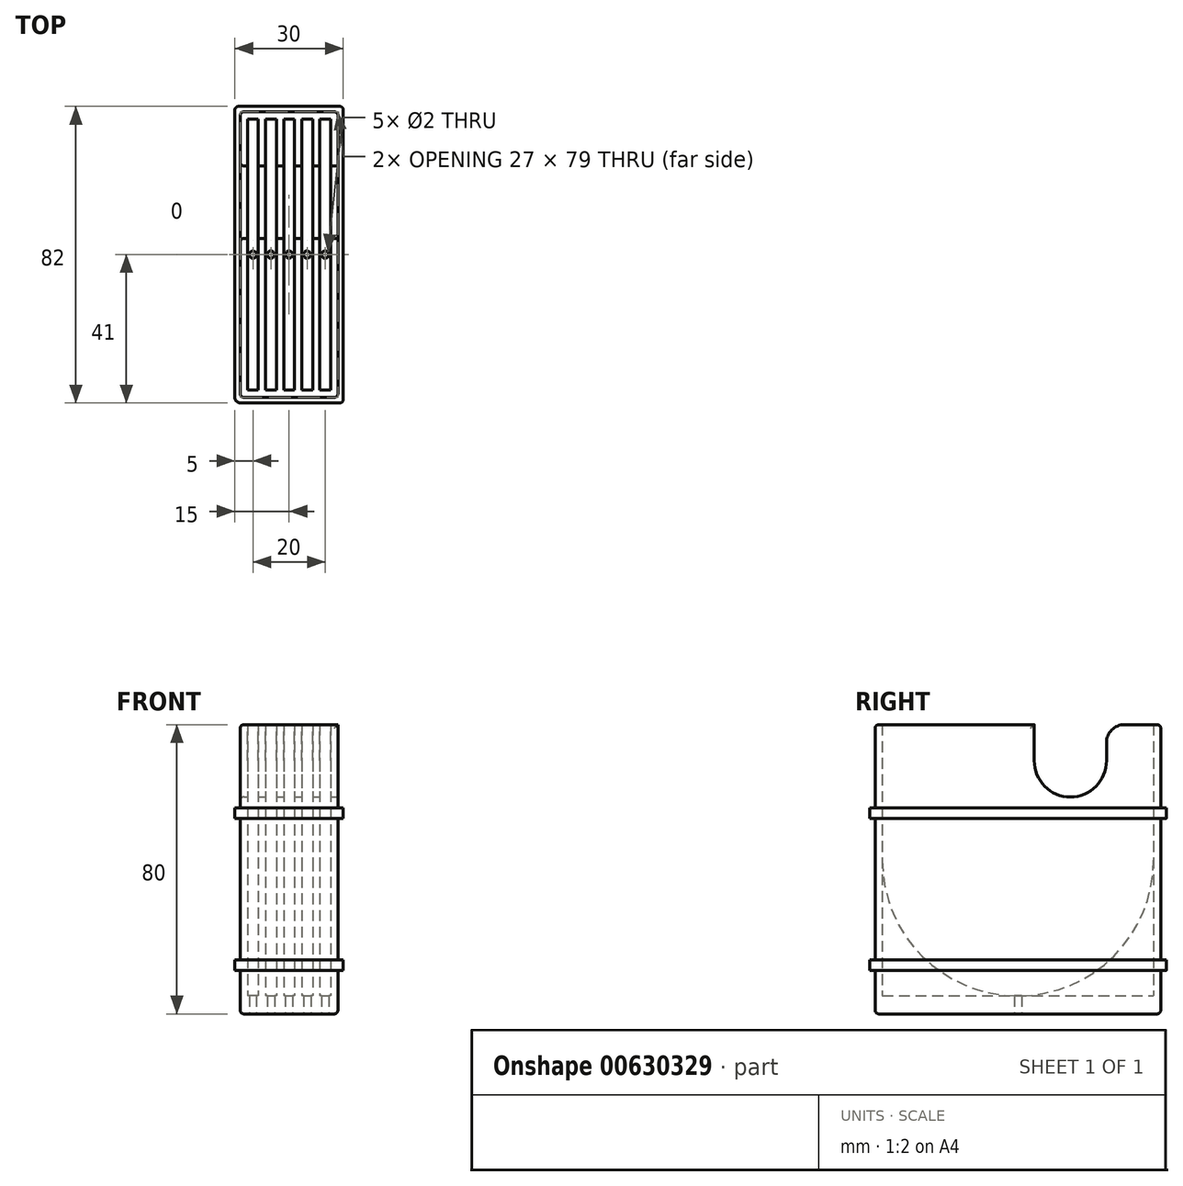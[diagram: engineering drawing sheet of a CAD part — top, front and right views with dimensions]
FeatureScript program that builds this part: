
annotation { "Feature Type Name" : "Feature", "Feature Type Description" : "" }
export const myFeature = defineFeature(function(context is Context, id is Id, definition is map)
    precondition{}
    {
        {
            var Q0;
            Q0=qCreatedBy(makeId("Top.planeOp"),FACE);
            var sketch = newSketch(context, id + "F0", { "sketchPlane" : qUnion([Q0])});
            skLineSegment(sketch, "E0.bottom", {"start": v(0, 0) * mm, "end": v(-3, 0) * mm});
            skLineSegment(sketch, "E0.top", {"start": v(0, 75) * mm, "end": v(-3, 75) * mm});
            skLineSegment(sketch, "E0.left", {"start": v(0, 0) * mm, "end": v(0, 75) * mm});
            skLineSegment(sketch, "E0.right", {"start": v(-3, 0) * mm, "end": v(-3, 75) * mm});
            skLineSegment(sketch, "E1.1.0.0", {"start": v(2, 0) * mm, "end": v(2, 75) * mm});
            skLineSegment(sketch, "E1.1.0.1", {"start": v(5, 75) * mm, "end": v(2, 75) * mm});
            skLineSegment(sketch, "E1.1.0.2", {"start": v(5, 0) * mm, "end": v(5, 75) * mm});
            skLineSegment(sketch, "E1.1.0.3", {"start": v(5, 0) * mm, "end": v(2, 0) * mm});
            skLineSegment(sketch, "E1.2.0.0", {"start": v(7, 0) * mm, "end": v(7, 75) * mm});
            skLineSegment(sketch, "E1.2.0.1", {"start": v(10, 75) * mm, "end": v(7, 75) * mm});
            skLineSegment(sketch, "E1.2.0.2", {"start": v(10, 0) * mm, "end": v(10, 75) * mm});
            skLineSegment(sketch, "E1.2.0.3", {"start": v(10, 0) * mm, "end": v(7, 0) * mm});
            skLineSegment(sketch, "E1.3.0.0", {"start": v(12, 0) * mm, "end": v(12, 75) * mm});
            skLineSegment(sketch, "E1.3.0.1", {"start": v(15, 75) * mm, "end": v(12, 75) * mm});
            skLineSegment(sketch, "E1.3.0.2", {"start": v(15, 0) * mm, "end": v(15, 75) * mm});
            skLineSegment(sketch, "E1.3.0.3", {"start": v(15, 0) * mm, "end": v(12, 0) * mm});
            skLineSegment(sketch, "E1.4.0.0", {"start": v(17, 0) * mm, "end": v(17, 75) * mm});
            skLineSegment(sketch, "E1.4.0.1", {"start": v(20, 75) * mm, "end": v(17, 75) * mm});
            skLineSegment(sketch, "E1.4.0.2", {"start": v(20, 0) * mm, "end": v(20, 75) * mm});
            skLineSegment(sketch, "E1.4.0.3", {"start": v(20, 0) * mm, "end": v(17, 0) * mm});
            skLineSegment(sketch, "E1.direction1", {"start": v(-3, 0) * mm, "end": v(2, 0) * mm, "construction": true});
            skLineSegment(sketch, "E2", {"start": v(-3, 0) * mm, "end": v(-5, 0) * mm, "construction": true});
            skLineSegment(sketch, "E3", {"start": v(-5, 0) * mm, "end": v(-5, -2) * mm, "construction": true});
            skLineSegment(sketch, "E4.bottom", {"start": v(-5, -2) * mm, "end": v(22, -2) * mm});
            skLineSegment(sketch, "E4.top", {"start": v(-5, 77) * mm, "end": v(22, 77) * mm});
            skLineSegment(sketch, "E4.left", {"start": v(-5, -2) * mm, "end": v(-5, 77) * mm});
            skLineSegment(sketch, "E4.right", {"start": v(22, -2) * mm, "end": v(22, 77) * mm});
            skSolve(sketch);
        }
        {
            var Q0;
            Q0=makeQuery(id+"F0.imprint","IMPRINT",FACE,{"disambiguationData":[TD([[makeQuery(id+"F0.imprint","IMPRINT",EDGE,{"derivedFrom":sQuery(id+"F0.wireOp",EDGE,"E0.bottom")}),1.0]])]});
            extrude(context, id + "F1", {"entities" : qUnion([Q0]), "depth" : 75 * mm, "offsetDistance" : 25 * mm});
        }
        {
            var Q0;
            Q0=qCreatedBy(makeId("Right.planeOp"),FACE);
            var sketch = newSketch(context, id + "F2", { "sketchPlane" : qUnion([Q0])});
            skArc(sketch, "E5", {"start": v(42, 65) * mm, "mid": v(52, 55) * mm, "end": v(62, 65) * mm});
            skLineSegment(sketch, "E6", {"start": v(42, 65) * mm, "end": v(42, 77.98) * mm});
            skLineSegment(sketch, "E7", {"start": v(42, 77.98) * mm, "end": v(62, 77.98) * mm});
            skLineSegment(sketch, "E8", {"start": v(62, 77.98) * mm, "end": v(62, 65) * mm});
            skSolve(sketch);
        }
        {
            var Q0;
            Q0 = qSketchRegion(id + "F2", true);
            extrude(context, id + "F3", {"entities" : qUnion([Q0]), "operationType" : NewBodyOperationType.REMOVE, "oppositeDirection" : true, "depth" : 25 * mm, "offsetDistance" : 25 * mm, "hasSecondDirection" : true, "secondDirectionOppositeDirection" : false, "secondDirectionDepth" : 25 * mm});
        }
        {
            var Q0;
            Q0=makeQuery(id+"F3.boolean.opBoolean","INTERSECT",EDGE,{"disambiguationData":[OD(1.0)],"derivedFrom":[makeQuery(id+"F1.opExtrude","CAP_FACE",FACE,{"disambiguationData":[OSD([sQuery(id+"F0.wireOp",EDGE,"E0.bottom"),sQuery(id+"F0.wireOp",EDGE,"E0.top"),sQuery(id+"F0.wireOp",EDGE,"E0.left"),sQuery(id+"F0.wireOp",EDGE,"E0.right"),sQuery(id+"F0.wireOp",EDGE,"E1.1.0.0"),sQuery(id+"F0.wireOp",EDGE,"E1.1.0.1"),sQuery(id+"F0.wireOp",EDGE,"E1.1.0.2"),sQuery(id+"F0.wireOp",EDGE,"E1.1.0.3"),sQuery(id+"F0.wireOp",EDGE,"E1.2.0.0"),sQuery(id+"F0.wireOp",EDGE,"E1.2.0.1"),sQuery(id+"F0.wireOp",EDGE,"E1.2.0.2"),sQuery(id+"F0.wireOp",EDGE,"E1.2.0.3"),sQuery(id+"F0.wireOp",EDGE,"E1.3.0.0"),sQuery(id+"F0.wireOp",EDGE,"E1.3.0.1"),sQuery(id+"F0.wireOp",EDGE,"E1.3.0.2"),sQuery(id+"F0.wireOp",EDGE,"E1.3.0.3"),sQuery(id+"F0.wireOp",EDGE,"E1.4.0.0"),sQuery(id+"F0.wireOp",EDGE,"E1.4.0.1"),sQuery(id+"F0.wireOp",EDGE,"E1.4.0.2"),sQuery(id+"F0.wireOp",EDGE,"E1.4.0.3"),sQuery(id+"F0.wireOp",EDGE,"E4.bottom"),sQuery(id+"F0.wireOp",EDGE,"E4.top"),sQuery(id+"F0.wireOp",EDGE,"E4.left"),sQuery(id+"F0.wireOp",EDGE,"E4.right")])],"isStart":false}),makeQuery(id+"F3.opExtrude","SWEPT_FACE",FACE,{"disambiguationData":[OSD([sQuery(id+"F2.wireOp",EDGE,"E8")])]})]});
            var Q1;
            Q1=makeQuery(id+"F3.boolean.opBoolean","INTERSECT",EDGE,{"disambiguationData":[OD(0.0)],"derivedFrom":[makeQuery(id+"F1.opExtrude","CAP_FACE",FACE,{"disambiguationData":[OSD([sQuery(id+"F0.wireOp",EDGE,"E0.bottom"),sQuery(id+"F0.wireOp",EDGE,"E0.top"),sQuery(id+"F0.wireOp",EDGE,"E0.left"),sQuery(id+"F0.wireOp",EDGE,"E0.right"),sQuery(id+"F0.wireOp",EDGE,"E1.1.0.0"),sQuery(id+"F0.wireOp",EDGE,"E1.1.0.1"),sQuery(id+"F0.wireOp",EDGE,"E1.1.0.2"),sQuery(id+"F0.wireOp",EDGE,"E1.1.0.3"),sQuery(id+"F0.wireOp",EDGE,"E1.2.0.0"),sQuery(id+"F0.wireOp",EDGE,"E1.2.0.1"),sQuery(id+"F0.wireOp",EDGE,"E1.2.0.2"),sQuery(id+"F0.wireOp",EDGE,"E1.2.0.3"),sQuery(id+"F0.wireOp",EDGE,"E1.3.0.0"),sQuery(id+"F0.wireOp",EDGE,"E1.3.0.1"),sQuery(id+"F0.wireOp",EDGE,"E1.3.0.2"),sQuery(id+"F0.wireOp",EDGE,"E1.3.0.3"),sQuery(id+"F0.wireOp",EDGE,"E1.4.0.0"),sQuery(id+"F0.wireOp",EDGE,"E1.4.0.1"),sQuery(id+"F0.wireOp",EDGE,"E1.4.0.2"),sQuery(id+"F0.wireOp",EDGE,"E1.4.0.3"),sQuery(id+"F0.wireOp",EDGE,"E4.bottom"),sQuery(id+"F0.wireOp",EDGE,"E4.top"),sQuery(id+"F0.wireOp",EDGE,"E4.left"),sQuery(id+"F0.wireOp",EDGE,"E4.right")])],"isStart":false}),makeQuery(id+"F3.opExtrude","SWEPT_FACE",FACE,{"disambiguationData":[OSD([sQuery(id+"F2.wireOp",EDGE,"E8")])]})]});
            var Q2;
            Q2=makeQuery(id+"F3.boolean.opBoolean","INTERSECT",EDGE,{"disambiguationData":[OD(2.0)],"derivedFrom":[makeQuery(id+"F1.opExtrude","CAP_FACE",FACE,{"disambiguationData":[OSD([sQuery(id+"F0.wireOp",EDGE,"E0.bottom"),sQuery(id+"F0.wireOp",EDGE,"E0.top"),sQuery(id+"F0.wireOp",EDGE,"E0.left"),sQuery(id+"F0.wireOp",EDGE,"E0.right"),sQuery(id+"F0.wireOp",EDGE,"E1.1.0.0"),sQuery(id+"F0.wireOp",EDGE,"E1.1.0.1"),sQuery(id+"F0.wireOp",EDGE,"E1.1.0.2"),sQuery(id+"F0.wireOp",EDGE,"E1.1.0.3"),sQuery(id+"F0.wireOp",EDGE,"E1.2.0.0"),sQuery(id+"F0.wireOp",EDGE,"E1.2.0.1"),sQuery(id+"F0.wireOp",EDGE,"E1.2.0.2"),sQuery(id+"F0.wireOp",EDGE,"E1.2.0.3"),sQuery(id+"F0.wireOp",EDGE,"E1.3.0.0"),sQuery(id+"F0.wireOp",EDGE,"E1.3.0.1"),sQuery(id+"F0.wireOp",EDGE,"E1.3.0.2"),sQuery(id+"F0.wireOp",EDGE,"E1.3.0.3"),sQuery(id+"F0.wireOp",EDGE,"E1.4.0.0"),sQuery(id+"F0.wireOp",EDGE,"E1.4.0.1"),sQuery(id+"F0.wireOp",EDGE,"E1.4.0.2"),sQuery(id+"F0.wireOp",EDGE,"E1.4.0.3"),sQuery(id+"F0.wireOp",EDGE,"E4.bottom"),sQuery(id+"F0.wireOp",EDGE,"E4.top"),sQuery(id+"F0.wireOp",EDGE,"E4.left"),sQuery(id+"F0.wireOp",EDGE,"E4.right")])],"isStart":false}),makeQuery(id+"F3.opExtrude","SWEPT_FACE",FACE,{"disambiguationData":[OSD([sQuery(id+"F2.wireOp",EDGE,"E8")])]})]});
            var Q3;
            Q3=makeQuery(id+"F3.boolean.opBoolean","INTERSECT",EDGE,{"disambiguationData":[OD(3.0)],"derivedFrom":[makeQuery(id+"F1.opExtrude","CAP_FACE",FACE,{"disambiguationData":[OSD([sQuery(id+"F0.wireOp",EDGE,"E0.bottom"),sQuery(id+"F0.wireOp",EDGE,"E0.top"),sQuery(id+"F0.wireOp",EDGE,"E0.left"),sQuery(id+"F0.wireOp",EDGE,"E0.right"),sQuery(id+"F0.wireOp",EDGE,"E1.1.0.0"),sQuery(id+"F0.wireOp",EDGE,"E1.1.0.1"),sQuery(id+"F0.wireOp",EDGE,"E1.1.0.2"),sQuery(id+"F0.wireOp",EDGE,"E1.1.0.3"),sQuery(id+"F0.wireOp",EDGE,"E1.2.0.0"),sQuery(id+"F0.wireOp",EDGE,"E1.2.0.1"),sQuery(id+"F0.wireOp",EDGE,"E1.2.0.2"),sQuery(id+"F0.wireOp",EDGE,"E1.2.0.3"),sQuery(id+"F0.wireOp",EDGE,"E1.3.0.0"),sQuery(id+"F0.wireOp",EDGE,"E1.3.0.1"),sQuery(id+"F0.wireOp",EDGE,"E1.3.0.2"),sQuery(id+"F0.wireOp",EDGE,"E1.3.0.3"),sQuery(id+"F0.wireOp",EDGE,"E1.4.0.0"),sQuery(id+"F0.wireOp",EDGE,"E1.4.0.1"),sQuery(id+"F0.wireOp",EDGE,"E1.4.0.2"),sQuery(id+"F0.wireOp",EDGE,"E1.4.0.3"),sQuery(id+"F0.wireOp",EDGE,"E4.bottom"),sQuery(id+"F0.wireOp",EDGE,"E4.top"),sQuery(id+"F0.wireOp",EDGE,"E4.left"),sQuery(id+"F0.wireOp",EDGE,"E4.right")])],"isStart":false}),makeQuery(id+"F3.opExtrude","SWEPT_FACE",FACE,{"disambiguationData":[OSD([sQuery(id+"F2.wireOp",EDGE,"E8")])]})]});
            var Q4;
            Q4=makeQuery(id+"F3.boolean.opBoolean","INTERSECT",EDGE,{"disambiguationData":[OD(4.0)],"derivedFrom":[makeQuery(id+"F1.opExtrude","CAP_FACE",FACE,{"disambiguationData":[OSD([sQuery(id+"F0.wireOp",EDGE,"E0.bottom"),sQuery(id+"F0.wireOp",EDGE,"E0.top"),sQuery(id+"F0.wireOp",EDGE,"E0.left"),sQuery(id+"F0.wireOp",EDGE,"E0.right"),sQuery(id+"F0.wireOp",EDGE,"E1.1.0.0"),sQuery(id+"F0.wireOp",EDGE,"E1.1.0.1"),sQuery(id+"F0.wireOp",EDGE,"E1.1.0.2"),sQuery(id+"F0.wireOp",EDGE,"E1.1.0.3"),sQuery(id+"F0.wireOp",EDGE,"E1.2.0.0"),sQuery(id+"F0.wireOp",EDGE,"E1.2.0.1"),sQuery(id+"F0.wireOp",EDGE,"E1.2.0.2"),sQuery(id+"F0.wireOp",EDGE,"E1.2.0.3"),sQuery(id+"F0.wireOp",EDGE,"E1.3.0.0"),sQuery(id+"F0.wireOp",EDGE,"E1.3.0.1"),sQuery(id+"F0.wireOp",EDGE,"E1.3.0.2"),sQuery(id+"F0.wireOp",EDGE,"E1.3.0.3"),sQuery(id+"F0.wireOp",EDGE,"E1.4.0.0"),sQuery(id+"F0.wireOp",EDGE,"E1.4.0.1"),sQuery(id+"F0.wireOp",EDGE,"E1.4.0.2"),sQuery(id+"F0.wireOp",EDGE,"E1.4.0.3"),sQuery(id+"F0.wireOp",EDGE,"E4.bottom"),sQuery(id+"F0.wireOp",EDGE,"E4.top"),sQuery(id+"F0.wireOp",EDGE,"E4.left"),sQuery(id+"F0.wireOp",EDGE,"E4.right")])],"isStart":false}),makeQuery(id+"F3.opExtrude","SWEPT_FACE",FACE,{"disambiguationData":[OSD([sQuery(id+"F2.wireOp",EDGE,"E8")])]})]});
            var Q5;
            Q5=makeQuery(id+"F3.boolean.opBoolean","INTERSECT",EDGE,{"disambiguationData":[OD(5.0)],"derivedFrom":[makeQuery(id+"F1.opExtrude","CAP_FACE",FACE,{"disambiguationData":[OSD([sQuery(id+"F0.wireOp",EDGE,"E0.bottom"),sQuery(id+"F0.wireOp",EDGE,"E0.top"),sQuery(id+"F0.wireOp",EDGE,"E0.left"),sQuery(id+"F0.wireOp",EDGE,"E0.right"),sQuery(id+"F0.wireOp",EDGE,"E1.1.0.0"),sQuery(id+"F0.wireOp",EDGE,"E1.1.0.1"),sQuery(id+"F0.wireOp",EDGE,"E1.1.0.2"),sQuery(id+"F0.wireOp",EDGE,"E1.1.0.3"),sQuery(id+"F0.wireOp",EDGE,"E1.2.0.0"),sQuery(id+"F0.wireOp",EDGE,"E1.2.0.1"),sQuery(id+"F0.wireOp",EDGE,"E1.2.0.2"),sQuery(id+"F0.wireOp",EDGE,"E1.2.0.3"),sQuery(id+"F0.wireOp",EDGE,"E1.3.0.0"),sQuery(id+"F0.wireOp",EDGE,"E1.3.0.1"),sQuery(id+"F0.wireOp",EDGE,"E1.3.0.2"),sQuery(id+"F0.wireOp",EDGE,"E1.3.0.3"),sQuery(id+"F0.wireOp",EDGE,"E1.4.0.0"),sQuery(id+"F0.wireOp",EDGE,"E1.4.0.1"),sQuery(id+"F0.wireOp",EDGE,"E1.4.0.2"),sQuery(id+"F0.wireOp",EDGE,"E1.4.0.3"),sQuery(id+"F0.wireOp",EDGE,"E4.bottom"),sQuery(id+"F0.wireOp",EDGE,"E4.top"),sQuery(id+"F0.wireOp",EDGE,"E4.left"),sQuery(id+"F0.wireOp",EDGE,"E4.right")])],"isStart":false}),makeQuery(id+"F3.opExtrude","SWEPT_FACE",FACE,{"disambiguationData":[OSD([sQuery(id+"F2.wireOp",EDGE,"E8")])]})]});
            fillet(context, id + "F4", {"entities" : qUnion([Q0, Q1, Q2, Q3, Q4, Q5]), "radius" : 5 * mm, "tangentPropagation" : true, "allowEdgeOverflow" : false});
        }
        {
            var Q0;
            Q0=qCreatedBy(makeId("Top.planeOp"),FACE);
            var sketch = newSketch(context, id + "F5", { "sketchPlane" : qUnion([Q0])});
            skLineSegment(sketch, "E9.bottom", {"start": v(-5, -2) * mm, "end": v(22, -2) * mm});
            skLineSegment(sketch, "E9.top", {"start": v(-5, 77) * mm, "end": v(22, 77) * mm});
            skLineSegment(sketch, "E9.left", {"start": v(-5, -2) * mm, "end": v(-5, 77) * mm});
            skLineSegment(sketch, "E9.right", {"start": v(22, -2) * mm, "end": v(22, 77) * mm});
            skSolve(sketch);
        }
        {
            var Q0;
            Q0 = qSketchRegion(id + "F5", true);
            extrude(context, id + "F6", {"entities" : qUnion([Q0]), "operationType" : NewBodyOperationType.ADD, "oppositeDirection" : true, "depth" : 5 * mm, "offsetDistance" : 25 * mm});
        }
        {
            var Q0;
            Q0=makeQuery(id+"F1.opExtrude","CAP_EDGE",EDGE,{"disambiguationData":[OSD([sQuery(id+"F0.wireOp",EDGE,"E1.4.0.3")])],"isStart":true});
            var Q1;
            Q1=makeQuery(id+"F1.opExtrude","CAP_EDGE",EDGE,{"disambiguationData":[OSD([sQuery(id+"F0.wireOp",EDGE,"E1.3.0.3")])],"isStart":true});
            var Q2;
            Q2=makeQuery(id+"F1.opExtrude","CAP_EDGE",EDGE,{"disambiguationData":[OSD([sQuery(id+"F0.wireOp",EDGE,"E1.2.0.3")])],"isStart":true});
            var Q3;
            Q3=makeQuery(id+"F1.opExtrude","CAP_EDGE",EDGE,{"disambiguationData":[OSD([sQuery(id+"F0.wireOp",EDGE,"E1.1.0.3")])],"isStart":true});
            var Q4;
            Q4=makeQuery(id+"F1.opExtrude","CAP_EDGE",EDGE,{"disambiguationData":[OSD([sQuery(id+"F0.wireOp",EDGE,"E0.bottom")])],"isStart":true});
            var Q5;
            Q5=makeQuery(id+"F1.opExtrude","CAP_EDGE",EDGE,{"disambiguationData":[OSD([sQuery(id+"F0.wireOp",EDGE,"E1.4.0.1")])],"isStart":true});
            var Q6;
            Q6=makeQuery(id+"F1.opExtrude","CAP_EDGE",EDGE,{"disambiguationData":[OSD([sQuery(id+"F0.wireOp",EDGE,"E1.2.0.1")])],"isStart":true});
            var Q7;
            Q7=makeQuery(id+"F1.opExtrude","CAP_EDGE",EDGE,{"disambiguationData":[OSD([sQuery(id+"F0.wireOp",EDGE,"E1.3.0.1")])],"isStart":true});
            var Q8;
            Q8=makeQuery(id+"F1.opExtrude","CAP_EDGE",EDGE,{"disambiguationData":[OSD([sQuery(id+"F0.wireOp",EDGE,"E1.1.0.1")])],"isStart":true});
            var Q9;
            Q9=makeQuery(id+"F1.opExtrude","CAP_EDGE",EDGE,{"disambiguationData":[OSD([sQuery(id+"F0.wireOp",EDGE,"E0.top")])],"isStart":true});
            fillet(context, id + "F7", {"entities" : qUnion([Q0, Q1, Q2, Q3, Q4, Q5, Q6, Q7, Q8, Q9]), "radius" : 37.5 * mm, "tangentPropagation" : true, "allowEdgeOverflow" : false});
        }
        {
            var Q0;
            Q0=qCreatedBy(makeId("Top.planeOp"),FACE);
            var sketch = newSketch(context, id + "F8", { "sketchPlane" : qUnion([Q0])});
            skLineSegment(sketch, "E10", {"start": v(0, 0) * mm, "end": v(-5, 0) * mm, "construction": true});
            skLineSegment(sketch, "E11", {"start": v(-5, 0) * mm, "end": v(-5, -2) * mm, "construction": true});
            skLineSegment(sketch, "E12", {"start": v(-5, -2) * mm, "end": v(-6.5, -2) * mm, "construction": true});
            skLineSegment(sketch, "E13", {"start": v(-6.5, -2) * mm, "end": v(-6.5, -3.5) * mm, "construction": true});
            skLineSegment(sketch, "E14", {"start": v(-5, -3.5) * mm, "end": v(22.5, -3.5) * mm});
            skLineSegment(sketch, "E15", {"start": v(23.5, -2.5) * mm, "end": v(23.5, 77.5) * mm});
            skLineSegment(sketch, "E16", {"start": v(22.5, 78.5) * mm, "end": v(-5.5, 78.5) * mm});
            skLineSegment(sketch, "E17", {"start": v(-6.5, 77.5) * mm, "end": v(-6.5, -2) * mm});
            skLineSegment(sketch, "E18.0", {"start": v(-1.5, 79) * mm, "end": v(-1.5, -4) * mm});
            skLineSegment(sketch, "E19.0", {"start": v(-3.9, 75.9) * mm, "end": v(-3.9, -0.9) * mm});
            skLineSegment(sketch, "E19.1", {"start": v(20.9, 75.9) * mm, "end": v(-3.9, 75.9) * mm});
            skLineSegment(sketch, "E19.2", {"start": v(20.9, -0.9) * mm, "end": v(20.9, 75.9) * mm});
            skLineSegment(sketch, "E19.3", {"start": v(-3.9, -0.9) * mm, "end": v(20.9, -0.9) * mm});
            skPoint(sketch, "E20.visualSharp", {"position": v(-6.5, -3.5) * mm});
            skArc(sketch, "E20.filletArc", {"start": v(-6.5, -2) * mm, "mid": v(-6.06, -3.06) * mm, "end": v(-5, -3.5) * mm});
            skPoint(sketch, "E21.visualSharp", {"position": v(23.5, -3.5) * mm});
            skArc(sketch, "E21.filletArc", {"start": v(22.5, -3.5) * mm, "mid": v(23.2, -3.2) * mm, "end": v(23.5, -2.5) * mm});
            skPoint(sketch, "E22.visualSharp", {"position": v(23.5, 78.5) * mm});
            skArc(sketch, "E22.filletArc", {"start": v(23.5, 77.5) * mm, "mid": v(23.2, 78.2) * mm, "end": v(22.5, 78.5) * mm});
            skPoint(sketch, "E23.visualSharp", {"position": v(-6.5, 78.5) * mm});
            skArc(sketch, "E23.filletArc", {"start": v(-5.5, 78.5) * mm, "mid": v(-6.2, 78.2) * mm, "end": v(-6.5, 77.5) * mm});
            skSolve(sketch);
        }
        {
            var Q0;
            Q0=makeQuery(id+"F6.boolean.opBoolean","MERGE",EDGE,{"derivedFrom":[makeQuery(id+"F1.opExtrude","SWEPT_EDGE",EDGE,{"disambiguationData":[OSD([sQuery(id+"F0.wireOp",EDGE,"E4.bottom"),sQuery(id+"F0.wireOp",EDGE,"E4.right")])]}),makeQuery(id+"F6.opExtrude","SWEPT_EDGE",EDGE,{"disambiguationData":[OSD([sQuery(id+"F5.wireOp",EDGE,"E9.bottom"),sQuery(id+"F5.wireOp",EDGE,"E9.right")])]})]});
            var Q1;
            Q1=makeQuery(id+"F6.boolean.opBoolean","MERGE",EDGE,{"derivedFrom":[makeQuery(id+"F1.opExtrude","SWEPT_EDGE",EDGE,{"disambiguationData":[OSD([sQuery(id+"F0.wireOp",EDGE,"E4.bottom"),sQuery(id+"F0.wireOp",EDGE,"E4.left")])]}),makeQuery(id+"F6.opExtrude","SWEPT_EDGE",EDGE,{"disambiguationData":[OSD([sQuery(id+"F5.wireOp",EDGE,"E9.bottom"),sQuery(id+"F5.wireOp",EDGE,"E9.left")])]})]});
            var Q2;
            Q2=makeQuery(id+"F6.boolean.opBoolean","MERGE",FACE,{"derivedFrom":[makeQuery(id+"F1.opExtrude","SWEPT_FACE",FACE,{"disambiguationData":[OSD([sQuery(id+"F0.wireOp",EDGE,"E4.left")])]}),makeQuery(id+"F6.opExtrude","SWEPT_FACE",FACE,{"disambiguationData":[OSD([sQuery(id+"F5.wireOp",EDGE,"E9.left")])]})]});
            var Q3;
            Q3=makeQuery(id+"F6.boolean.opBoolean","MERGE",EDGE,{"derivedFrom":[makeQuery(id+"F1.opExtrude","SWEPT_EDGE",EDGE,{"disambiguationData":[OSD([sQuery(id+"F0.wireOp",EDGE,"E4.top"),sQuery(id+"F0.wireOp",EDGE,"E4.right")])]}),makeQuery(id+"F6.opExtrude","SWEPT_EDGE",EDGE,{"disambiguationData":[OSD([sQuery(id+"F5.wireOp",EDGE,"E9.top"),sQuery(id+"F5.wireOp",EDGE,"E9.right")])]})]});
            var Q4;
            {var subQ0=sQuery(id+"F0.wireOp",EDGE,"E4.right");var subQ1=sQuery(id+"F0.wireOp",EDGE,"E4.bottom");Q4=makeQuery(id+"F3.boolean.opBoolean","SPLIT",EDGE,{"disambiguationData":[TD([makeQuery(id+"F1.opExtrude","SWEPT_FACE",FACE,{"disambiguationData":[OSD([subQ1])]})])],"derivedFrom":makeQuery(id+"F1.opExtrude","CAP_EDGE",EDGE,{"disambiguationData":[OSD([subQ0])],"isStart":false})});}
            var Q5;
            Q5=makeQuery(id+"F1.opExtrude","CAP_EDGE",EDGE,{"disambiguationData":[OSD([sQuery(id+"F0.wireOp",EDGE,"E4.bottom")])],"isStart":false});
            var Q6;
            Q6=makeQuery(id+"F1.opExtrude","CAP_EDGE",EDGE,{"disambiguationData":[OSD([sQuery(id+"F0.wireOp",EDGE,"E4.top")])],"isStart":false});
            fillet(context, id + "F9", {"entities" : qUnion([Q0, Q1, Q2, Q3, Q4, Q5, Q6]), "radius" : 1 * mm, "tangentPropagation" : true, "allowEdgeOverflow" : false});
        }
        {
            var Q0;
            Q0 = qSketchRegion(id + "F8", true);
            extrude(context, id + "F10", {"entities" : qUnion([Q0]), "operationType" : NewBodyOperationType.ADD, "depth" : 10 * mm, "offsetDistance" : 25 * mm, "hasSecondDirection" : true, "secondDirectionOppositeDirection" : false, "secondDirectionDepth" : 7 * mm});
        }
        {
            var Q0;
            Q0 = qSketchRegion(id + "F8", true);
            extrude(context, id + "F11", {"entities" : qUnion([Q0]), "operationType" : NewBodyOperationType.ADD, "depth" : 52 * mm, "offsetDistance" : 25 * mm, "hasSecondDirection" : true, "secondDirectionOppositeDirection" : false, "secondDirectionDepth" : 49 * mm});
        }
        {
            var Q0;
            Q0=qCreatedBy(makeId("Top.planeOp"),FACE);
            var sketch = newSketch(context, id + "F12", { "sketchPlane" : qUnion([Q0])});
            skLineSegment(sketch, "E24", {"start": v(0, 0) * mm, "end": v(-1.5, 0) * mm, "construction": true});
            skLineSegment(sketch, "E25", {"start": v(-1.5, 0) * mm, "end": v(-1.5, 37.5) * mm, "construction": true});
            skLineSegment(sketch, "E26", {"start": v(-1.5, 37.5) * mm, "end": v(38.5, 37.5) * mm, "construction": true});
            skCircle(sketch, "E27", {"center": v(-1.5, 37.5) * mm, "radius": 1 * mm});
            skCircle(sketch, "E28.1.0.0", {"center": v(3.5, 37.5) * mm, "radius": 1 * mm});
            skCircle(sketch, "E28.2.0.0", {"center": v(8.5, 37.5) * mm, "radius": 1 * mm});
            skCircle(sketch, "E28.3.0.0", {"center": v(13.5, 37.5) * mm, "radius": 1 * mm});
            skCircle(sketch, "E28.4.0.0", {"center": v(18.5, 37.5) * mm, "radius": 1 * mm});
            skLineSegment(sketch, "E28.direction1", {"start": v(-1.5, 37.5) * mm, "end": v(3.5, 37.5) * mm, "construction": true});
            skSolve(sketch);
        }
        {
            var Q0;
            Q0 = qSketchRegion(id + "F12", true);
            extrude(context, id + "F13", {"entities" : qUnion([Q0]), "operationType" : NewBodyOperationType.REMOVE, "depth" : 25 * mm, "offsetDistance" : 25 * mm, "hasSecondDirection" : true, "secondDirectionOppositeDirection" : true, "secondDirectionDepth" : 25 * mm});
        }
        {
            var Q0;
            Q0=makeQuery(id+"F6.opExtrude","CAP_EDGE",EDGE,{"disambiguationData":[OSD([sQuery(id+"F5.wireOp",EDGE,"E9.right")])],"isStart":false});
            var Q1;
            {var subQ0=sQuery(id+"F5.wireOp",EDGE,"E9.left");Q1=makeQuery(id+"F9.opFillet","BLEND_EDGE",EDGE,{"blendedFrom":[makeQuery(id+"F6.opExtrude","CAP_EDGE",EDGE,{"disambiguationData":[OSD([subQ0])],"isStart":false}),makeQuery(id+"F6.opExtrude","CAP_FACE",FACE,{"disambiguationData":[OSD([sQuery(id+"F5.wireOp",EDGE,"E9.bottom"),sQuery(id+"F5.wireOp",EDGE,"E9.top"),subQ0,sQuery(id+"F5.wireOp",EDGE,"E9.right")])],"isStart":false})],"blendedInto":[makeQuery(id+"F6.opExtrude","CAP_FACE",FACE,{"disambiguationData":[OSD([sQuery(id+"F5.wireOp",EDGE,"E9.bottom"),sQuery(id+"F5.wireOp",EDGE,"E9.top"),subQ0,sQuery(id+"F5.wireOp",EDGE,"E9.right")])],"isStart":false})]});}
            fillet(context, id + "F14", {"entities" : qUnion([Q0, Q1]), "radius" : 1 * mm, "tangentPropagation" : true, "allowEdgeOverflow" : false});
        }
    });
